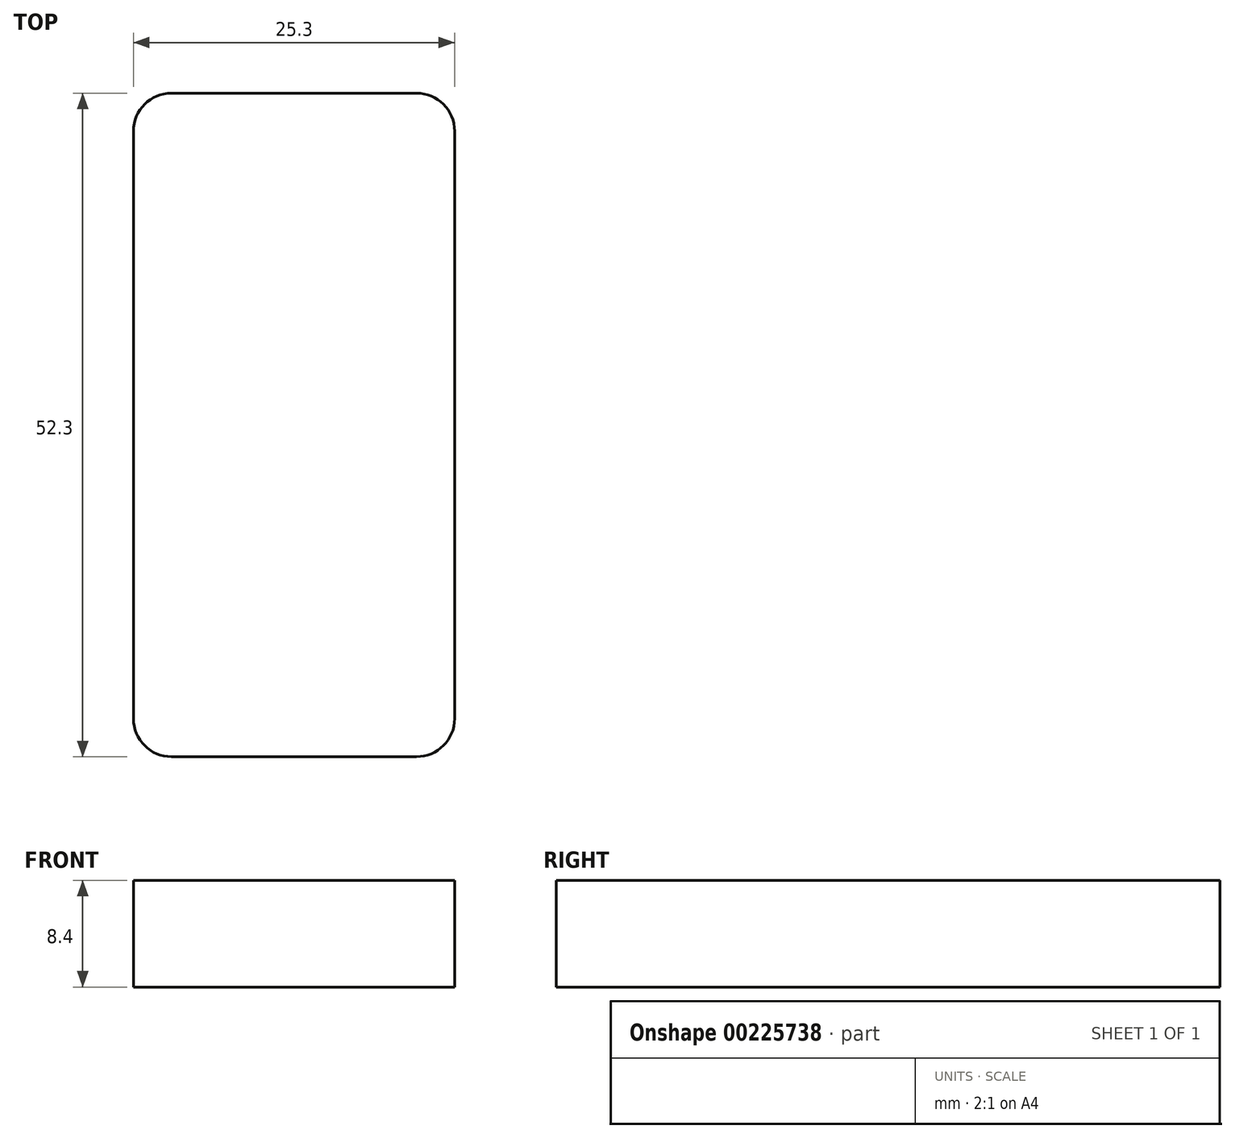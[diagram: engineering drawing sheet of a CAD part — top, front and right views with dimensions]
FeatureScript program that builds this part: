
annotation { "Feature Type Name" : "Feature", "Feature Type Description" : "" }
export const myFeature = defineFeature(function(context is Context, id is Id, definition is map)
    precondition{}
    {
        {
            var Q0;
            Q0=qCreatedBy(makeId("Top.planeOp"),FACE);
            var sketch = newSketch(context, id + "F0", { "sketchPlane" : qUnion([Q0])});
            skLineSegment(sketch, "E0.bottom", {"start": v(12.65, 26.15) * mm, "end": v(-12.65, 26.15) * mm});
            skLineSegment(sketch, "E0.top", {"start": v(12.65, -26.15) * mm, "end": v(-12.65, -26.15) * mm});
            skLineSegment(sketch, "E0.left", {"start": v(12.65, 26.15) * mm, "end": v(12.65, -26.15) * mm});
            skLineSegment(sketch, "E0.right", {"start": v(-12.65, 26.15) * mm, "end": v(-12.65, -26.15) * mm});
            skPoint(sketch, "E0.middle", {"position": v(0, 0) * mm});
            skSolve(sketch);
        }
        {
            var Q0;
            Q0=qSketchRegion(id+"F0",true);
            extrude(context, id + "F1", {"entities" : qUnion([Q0]), "depth" : 8.4 * mm});
        }
        {
            var Q0;
            Q0=makeQuery(id+"F1.opExtrude","SWEPT_EDGE",EDGE,{"disambiguationData":[OSD([sQuery(id+"F0.wireOp",EDGE,"E0.top"),sQuery(id+"F0.wireOp",EDGE,"E0.left")])]});
            var Q1;
            Q1=makeQuery(id+"F1.opExtrude","SWEPT_EDGE",EDGE,{"disambiguationData":[OSD([sQuery(id+"F0.wireOp",EDGE,"E0.bottom"),sQuery(id+"F0.wireOp",EDGE,"E0.left")])]});
            var Q2;
            Q2=makeQuery(id+"F1.opExtrude","SWEPT_EDGE",EDGE,{"disambiguationData":[OSD([sQuery(id+"F0.wireOp",EDGE,"E0.bottom"),sQuery(id+"F0.wireOp",EDGE,"E0.right")])]});
            var Q3;
            Q3=makeQuery(id+"F1.opExtrude","SWEPT_EDGE",EDGE,{"disambiguationData":[OSD([sQuery(id+"F0.wireOp",EDGE,"E0.top"),sQuery(id+"F0.wireOp",EDGE,"E0.right")])]});
            fillet(context, id + "F2", {"entities" : qUnion([Q0, Q1, Q2, Q3]), "radius" : 3 * mm, "tangentPropagation" : true, "allowEdgeOverflow" : false});
        }
    });
